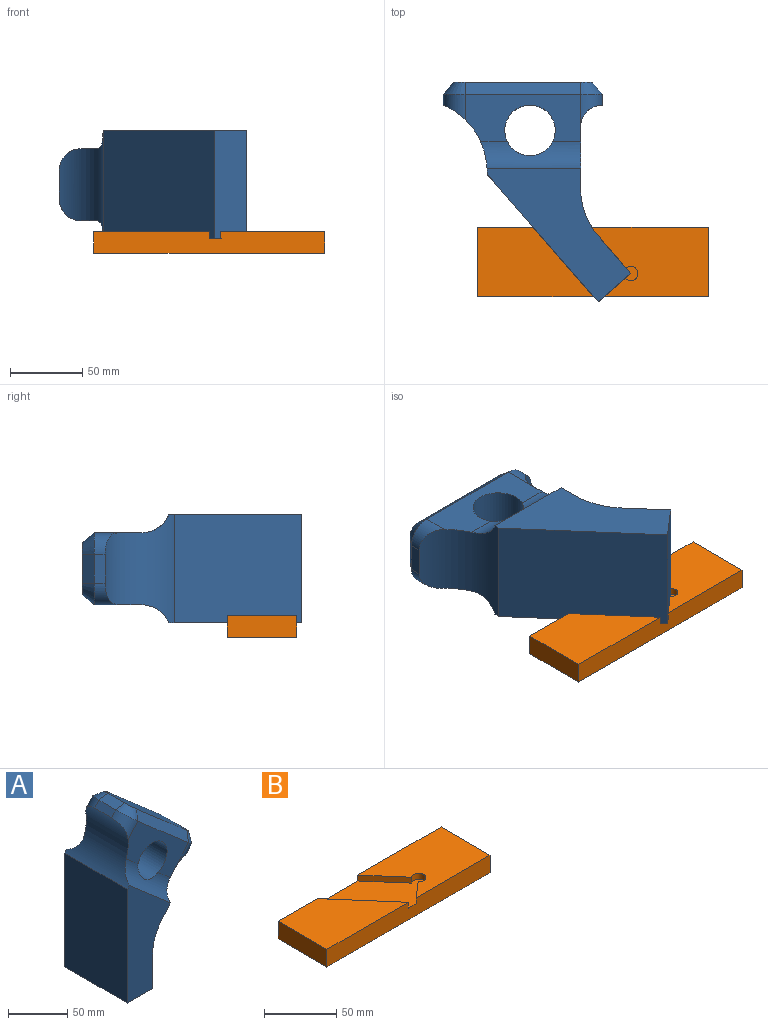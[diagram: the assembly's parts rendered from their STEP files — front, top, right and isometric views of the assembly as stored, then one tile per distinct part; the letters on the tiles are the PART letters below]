
ASSEMBLY  parts=2 mates=1
PART A: 31 faces, bbox 97.5x75x180.6 mm
  f0: plane 72.45x62.98mm, normal (0.66,0,0.75), area 3401.1mm2, adj f23,f24,f25,f26,f27,f28,f29,f30
  f1: plane 20x5.72mm, normal (-0.75,0,0.66), area 151.6mm2, adj f4,f21,f22,f25
  f2: plane 75x32.36mm, normal (0.75,0,-0.66), area 2619mm2, adj f5,f6,f10,f11,f17,f18,f19,f20
  f3: plane 20x5.78mm, normal (0.75,0,-0.66), area 153.2mm2, adj f6,f18,f20,f28
  f4: cylinder r=50mm len=75mm, axis (0,1,0), area 3117.6mm2, adj f1,f5,f7,f10,f12,f13,f15,f16
  f5: plane 120.13x51.37mm, normal (0,1,0), area 3771.3mm2, adj f2,f4,f7,f8,f9,f11,f15,f19
  f6: cylinder r=15mm len=50mm, axis (0,-1,0), area 1072mm2, adj f2,f3,f18,f20
  f7: plane 117.33x75mm, normal (-1,0,0), area 8799.6mm2, adj f4,f5,f8,f10
  f8: plane 75x30mm, normal (0,0,-1), area 2250mm2, adj f5,f7,f9,f10
  f9: plane 75x34.31mm, normal (1,0,0), area 2572.9mm2, adj f5,f8,f10,f11
  f10: plane 120.13x51.37mm, normal (0,-1,0), area 3771.3mm2, adj f2,f4,f7,f8,f9,f11,f16,f17
  f11: cylinder r=50mm len=75mm, axis (0,-1,0), area 2683.4mm2, adj f2,f5,f9,f10
  f12: plane 77.48x73.87mm, normal (0,1,0), area 1803.2mm2, adj f4,f14,f15,f20,f21,f29
  f13: plane 77.48x73.87mm, normal (0,-1,0), area 1803.2mm2, adj f4,f14,f16,f18,f22,f24
  f14: cylinder r=17.5mm len=54.85mm, axis (0,-1,0), area 5592.7mm2, adj f12,f13,f15,f16
  f15: cylinder r=20mm len=64.3mm, axis (0.75,0,-0.66), area 1348.4mm2, adj f4,f5,f12,f14,f19
  f16: cylinder r=20mm len=64.3mm, axis (-0.75,0,0.66), area 1348.4mm2, adj f4,f10,f13,f14,f17
  f17: torus R=35mm, axis (-0.75,0,0.66), area 1.8mm2, adj f2,f10,f16,f18
  f18: cylinder r=15mm len=34.83mm, axis (-0.66,0,-0.75), area 233.5mm2, adj f2,f3,f6,f13,f17,f26
  f19: torus R=35mm, axis (-0.75,0,0.66), area 1.8mm2, adj f2,f5,f15,f20
  f20: cylinder r=15mm len=34.83mm, axis (0.66,0,0.75), area 233.5mm2, adj f2,f3,f6,f12,f19,f30
  f21: cylinder r=15mm len=23.09mm, axis (-0.66,0,-0.75), area 251.5mm2, adj f1,f4,f12,f27
  f22: cylinder r=15mm len=23.09mm, axis (0.66,0,0.75), area 251.5mm2, adj f1,f4,f13,f23
  f23: cone r=8mm half-angle=40deg, axis (-0.66,0,-0.75), area 196.7mm2, adj f0,f22,f24,f25
  f24: plane 65.85x58.78mm, normal (0.42,-0.77,0.49), area 871.2mm2, adj f0,f13,f23,f26
  f25: plane 20x10.76mm, normal (-0.16,0,0.99), area 217.8mm2, adj f0,f1,f23,f27
  f26: cone r=8mm half-angle=40deg, axis (-0.66,0,-0.75), area 196.7mm2, adj f0,f18,f24,f28
  f27: cone r=8mm half-angle=40deg, axis (-0.66,0,-0.75), area 196.7mm2, adj f0,f21,f25,f29
  f28: plane 20x10.89mm, normal (1,0,-0.02), area 217.8mm2, adj f0,f3,f26,f30
  f29: plane 65.85x58.78mm, normal (0.42,0.77,0.49), area 871.2mm2, adj f0,f12,f27,f30
  f30: cone r=8mm half-angle=40deg, axis (-0.66,0,-0.75), area 196.7mm2, adj f0,f20,f28,f29
PART B: 12 faces, bbox 160x48x15 mm
  f0: plane 81.71x48mm, normal (0,0,1), area 3121.6mm2, adj f1,f2,f3,f7,f8,f9
  f1: plane 160x15mm, normal (0,-1,0), area 2361.9mm2, adj f0,f2,f4,f5,f6,f7,f10,f11
  f2: plane 48x15mm, normal (1,0,0), area 720mm2, adj f0,f1,f3,f6
  f3: plane 160x15mm, normal (0,1,0), area 2199.9mm2, adj f0,f2,f4,f5,f6,f9,f10,f11
  f4: plane 48x15mm, normal (-1,0,0), area 720mm2, adj f1,f3,f5,f6
  f5: plane 80x48mm, normal (0,0,1), area 2838.6mm2, adj f1,f3,f4,f10
  f6: plane 160x48mm, normal (0,0,-1), area 7680mm2, adj f1,f2,f3,f4
  f7: plane 14.68x12.76mm, normal (-0.66,0.75,0), area 97.2mm2, adj f0,f1,f8,f11
  f8: cylinder r=5mm len=10mm, axis (0,0,1), area 117.8mm2, adj f0,f7,f9,f11
  f9: plane 28.19x24.5mm, normal (-0.75,-0.66,0), area 186.7mm2, adj f0,f3,f8,f11
  f10: plane 48x41.73mm, normal (0.75,0.66,0), area 318mm2, adj f1,f3,f5,f11
  f11: plane 72.8x48mm, normal (0,0,1), area 1719.9mm2, adj f1,f3,f7,f8,f9,f10
PLACE A rot(axis=(-0.88,-0.33,0.33),97deg) t=(21.18,30.11,71.5)mm
PLACE B t=(17.75,57.75,61.5)mm
MATE revolute A.f5 <-> B.f8  axis (0,0,-1) through (43.82,49.79,71.5)mm
